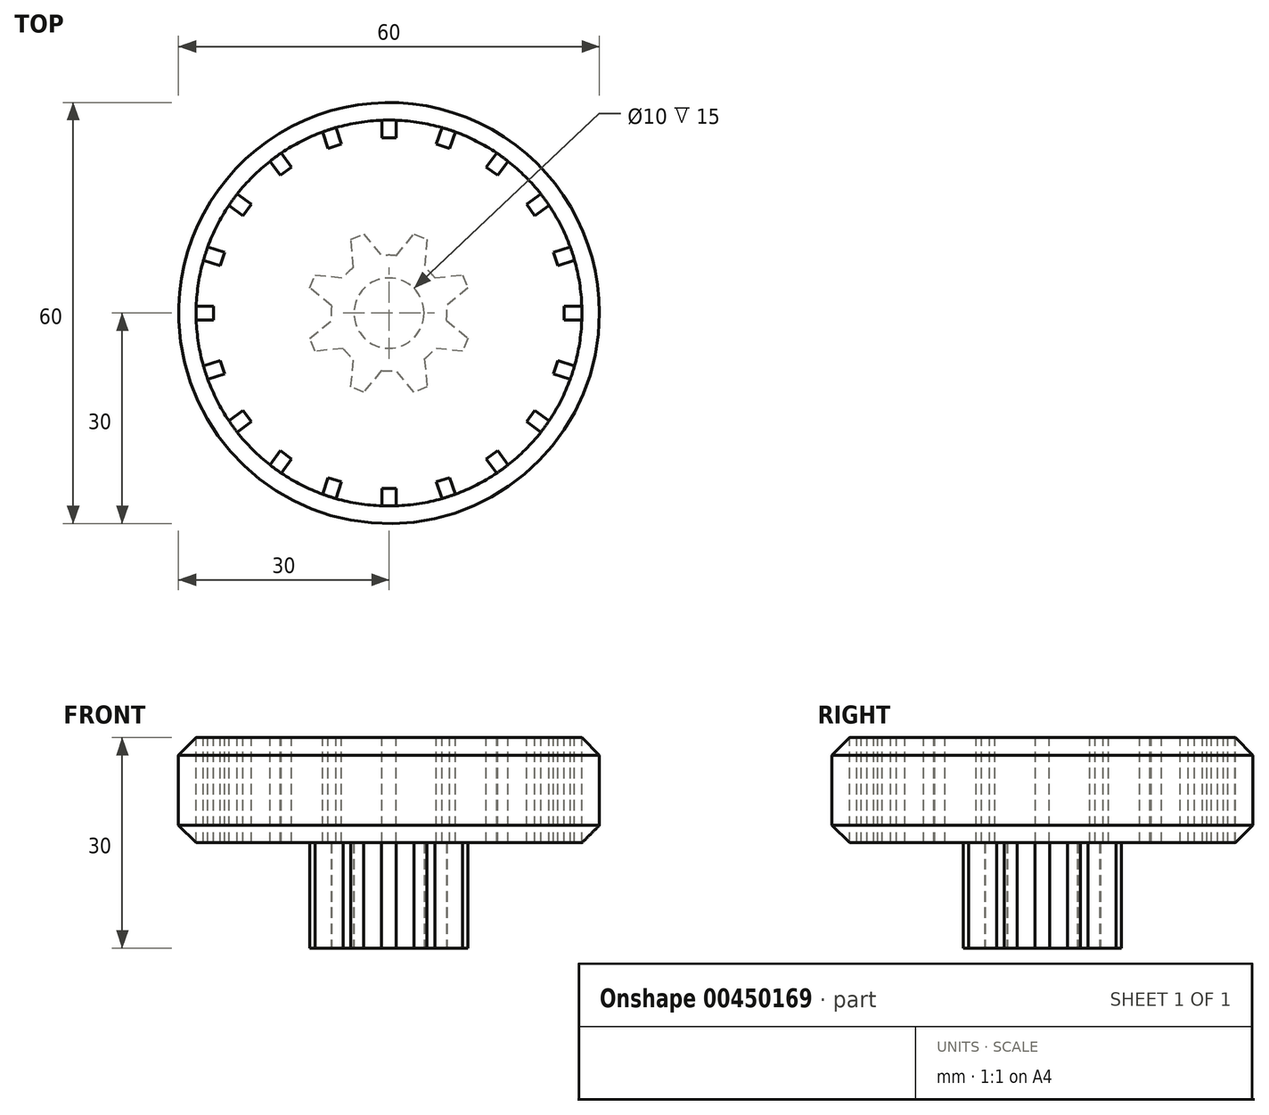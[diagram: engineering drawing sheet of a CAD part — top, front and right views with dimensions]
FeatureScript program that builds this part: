
annotation { "Feature Type Name" : "Feature", "Feature Type Description" : "" }
export const myFeature = defineFeature(function(context is Context, id is Id, definition is map)
    precondition{}
    {
        {
            var Q0;
            Q0=qCreatedBy(makeId("Top.planeOp"),FACE);
            var sketch = newSketch(context, id + "F0", { "sketchPlane" : qUnion([Q0])});
            skLineSegment(sketch, "E0", {"start": v(-8.18, 1.05) * mm, "end": v(-11.27, 3.59) * mm});
            skLineSegment(sketch, "E1", {"start": v(-11.27, 3.59) * mm, "end": v(-10.5, 5.43) * mm});
            skLineSegment(sketch, "E2", {"start": v(-10.5, 5.43) * mm, "end": v(-6.53, 5.05) * mm});
            skCircle(sketch, "E3", {"center": v(0, 0) * mm, "radius": 10 * mm, "construction": true});
            skPoint(sketch, "E4", {"position": v(-8.52, 5.24) * mm});
            skPoint(sketch, "E5", {"position": v(-9.73, 2.32) * mm});
            skArc(sketch, "E6", {"start": v(-5.05, 6.53) * mm, "mid": v(-5.83, 5.83) * mm, "end": v(-6.53, 5.05) * mm});
            skPoint(sketch, "E7", {"position": v(-11.82, 0) * mm});
            skLineSegment(sketch, "E8.1.0", {"start": v(-6.53, -5.05) * mm, "end": v(-10.5, -5.43) * mm});
            skLineSegment(sketch, "E8.1.1", {"start": v(-11.27, -3.59) * mm, "end": v(-8.18, -1.05) * mm});
            skArc(sketch, "E8.1.2", {"start": v(-8.18, 1.05) * mm, "mid": v(-8.25, 0) * mm, "end": v(-8.18, -1.05) * mm});
            skPoint(sketch, "E8.1.3", {"position": v(-9.73, -2.32) * mm});
            skPoint(sketch, "E8.1.4", {"position": v(-8.52, -5.24) * mm});
            skPoint(sketch, "E8.1.5", {"position": v(-8.36, -8.36) * mm});
            skLineSegment(sketch, "E8.1.6", {"start": v(-10.5, -5.43) * mm, "end": v(-11.27, -3.59) * mm});
            skLineSegment(sketch, "E8.2.0", {"start": v(-1.05, -8.18) * mm, "end": v(-3.59, -11.27) * mm});
            skLineSegment(sketch, "E8.2.1", {"start": v(-5.43, -10.5) * mm, "end": v(-5.05, -6.53) * mm});
            skArc(sketch, "E8.2.2", {"start": v(-6.53, -5.05) * mm, "mid": v(-5.83, -5.83) * mm, "end": v(-5.05, -6.53) * mm});
            skPoint(sketch, "E8.2.3", {"position": v(-5.24, -8.52) * mm});
            skPoint(sketch, "E8.2.4", {"position": v(-2.32, -9.73) * mm});
            skPoint(sketch, "E8.2.5", {"position": v(0, -11.82) * mm});
            skLineSegment(sketch, "E8.2.6", {"start": v(-3.59, -11.27) * mm, "end": v(-5.43, -10.5) * mm});
            skLineSegment(sketch, "E8.3.0", {"start": v(5.05, -6.53) * mm, "end": v(5.43, -10.5) * mm});
            skLineSegment(sketch, "E8.3.1", {"start": v(3.59, -11.27) * mm, "end": v(1.05, -8.18) * mm});
            skArc(sketch, "E8.3.2", {"start": v(-1.05, -8.18) * mm, "mid": v(0, -8.25) * mm, "end": v(1.05, -8.18) * mm});
            skPoint(sketch, "E8.3.3", {"position": v(2.32, -9.73) * mm});
            skPoint(sketch, "E8.3.4", {"position": v(5.24, -8.52) * mm});
            skPoint(sketch, "E8.3.5", {"position": v(8.36, -8.36) * mm});
            skLineSegment(sketch, "E8.3.6", {"start": v(5.43, -10.5) * mm, "end": v(3.59, -11.27) * mm});
            skLineSegment(sketch, "E8.4.0", {"start": v(8.18, -1.05) * mm, "end": v(11.27, -3.59) * mm});
            skLineSegment(sketch, "E8.4.1", {"start": v(10.5, -5.43) * mm, "end": v(6.53, -5.05) * mm});
            skArc(sketch, "E8.4.2", {"start": v(5.05, -6.53) * mm, "mid": v(5.83, -5.83) * mm, "end": v(6.53, -5.05) * mm});
            skPoint(sketch, "E8.4.3", {"position": v(8.52, -5.24) * mm});
            skPoint(sketch, "E8.4.4", {"position": v(9.73, -2.32) * mm});
            skPoint(sketch, "E8.4.5", {"position": v(11.82, 0) * mm});
            skLineSegment(sketch, "E8.4.6", {"start": v(11.27, -3.59) * mm, "end": v(10.5, -5.43) * mm});
            skLineSegment(sketch, "E8.5.0", {"start": v(6.53, 5.05) * mm, "end": v(10.5, 5.43) * mm});
            skLineSegment(sketch, "E8.5.1", {"start": v(11.27, 3.59) * mm, "end": v(8.18, 1.05) * mm});
            skArc(sketch, "E8.5.2", {"start": v(8.18, -1.05) * mm, "mid": v(8.25, 0) * mm, "end": v(8.18, 1.05) * mm});
            skPoint(sketch, "E8.5.3", {"position": v(9.73, 2.32) * mm});
            skPoint(sketch, "E8.5.4", {"position": v(8.52, 5.24) * mm});
            skPoint(sketch, "E8.5.5", {"position": v(8.36, 8.36) * mm});
            skLineSegment(sketch, "E8.5.6", {"start": v(10.5, 5.43) * mm, "end": v(11.27, 3.59) * mm});
            skLineSegment(sketch, "E8.6.0", {"start": v(1.05, 8.18) * mm, "end": v(3.59, 11.27) * mm});
            skLineSegment(sketch, "E8.6.1", {"start": v(5.43, 10.5) * mm, "end": v(5.05, 6.53) * mm});
            skArc(sketch, "E8.6.2", {"start": v(6.53, 5.05) * mm, "mid": v(5.83, 5.83) * mm, "end": v(5.05, 6.53) * mm});
            skPoint(sketch, "E8.6.3", {"position": v(5.24, 8.52) * mm});
            skPoint(sketch, "E8.6.4", {"position": v(2.32, 9.73) * mm});
            skPoint(sketch, "E8.6.5", {"position": v(0, 11.82) * mm});
            skLineSegment(sketch, "E8.6.6", {"start": v(3.59, 11.27) * mm, "end": v(5.43, 10.5) * mm});
            skLineSegment(sketch, "E8.7.0", {"start": v(-5.05, 6.53) * mm, "end": v(-5.43, 10.5) * mm});
            skLineSegment(sketch, "E8.7.1", {"start": v(-3.59, 11.27) * mm, "end": v(-1.05, 8.18) * mm});
            skArc(sketch, "E8.7.2", {"start": v(1.05, 8.18) * mm, "mid": v(0, 8.25) * mm, "end": v(-1.05, 8.18) * mm});
            skPoint(sketch, "E8.7.3", {"position": v(-2.32, 9.73) * mm});
            skPoint(sketch, "E8.7.4", {"position": v(-5.24, 8.52) * mm});
            skPoint(sketch, "E8.7.5", {"position": v(-8.36, 8.36) * mm});
            skLineSegment(sketch, "E8.7.6", {"start": v(-5.43, 10.5) * mm, "end": v(-3.59, 11.27) * mm});
            skCircle(sketch, "E9", {"center": v(0, 0) * mm, "radius": 5 * mm});
            skCircle(sketch, "E10", {"center": v(0, 0) * mm, "radius": 4.5 * mm});
            skPoint(sketch, "E11", {"position": v(0, 8.25) * mm});
            skSolve(sketch);
        }
        {
            var Q0;
            Q0=qSketchRegion(id+"F0",true);
            extrude(context, id + "F1", {"entities" : qUnion([Q0]), "endBound" : BoundingType.SYMMETRIC, "depth" : 15 * mm});
        }
        {
            var Q0;
            {var subQ0=sQuery(id+"F0.wireOp",EDGE,"E9");Q0=makeQuery(id+"FjRsnNbBz0NxSXN_1.boolean.opBoolean","MERGE",FACE,{"derivedFrom":[makeQuery(id+"F1.opExtrude","CAP_FACE",FACE,{"disambiguationData":[OSD([sQuery(id+"F0.wireOp",EDGE,"E0"),sQuery(id+"F0.wireOp",EDGE,"E1"),sQuery(id+"F0.wireOp",EDGE,"E2"),sQuery(id+"F0.wireOp",EDGE,"E6"),sQuery(id+"F0.wireOp",EDGE,"E8.1.0"),sQuery(id+"F0.wireOp",EDGE,"E8.1.1"),sQuery(id+"F0.wireOp",EDGE,"E8.1.2"),sQuery(id+"F0.wireOp",EDGE,"E8.1.6"),sQuery(id+"F0.wireOp",EDGE,"E8.2.0"),sQuery(id+"F0.wireOp",EDGE,"E8.2.1"),sQuery(id+"F0.wireOp",EDGE,"E8.2.2"),sQuery(id+"F0.wireOp",EDGE,"E8.2.6"),sQuery(id+"F0.wireOp",EDGE,"E8.3.0"),sQuery(id+"F0.wireOp",EDGE,"E8.3.1"),sQuery(id+"F0.wireOp",EDGE,"E8.3.2"),sQuery(id+"F0.wireOp",EDGE,"E8.3.6"),sQuery(id+"F0.wireOp",EDGE,"E8.4.0"),sQuery(id+"F0.wireOp",EDGE,"E8.4.1"),sQuery(id+"F0.wireOp",EDGE,"E8.4.2"),sQuery(id+"F0.wireOp",EDGE,"E8.4.6"),sQuery(id+"F0.wireOp",EDGE,"E8.5.0"),sQuery(id+"F0.wireOp",EDGE,"E8.5.1"),sQuery(id+"F0.wireOp",EDGE,"E8.5.2"),sQuery(id+"F0.wireOp",EDGE,"E8.5.6"),sQuery(id+"F0.wireOp",EDGE,"E8.6.0"),sQuery(id+"F0.wireOp",EDGE,"E8.6.1"),sQuery(id+"F0.wireOp",EDGE,"E8.6.2"),sQuery(id+"F0.wireOp",EDGE,"E8.6.6"),sQuery(id+"F0.wireOp",EDGE,"E8.7.0"),sQuery(id+"F0.wireOp",EDGE,"E8.7.1"),sQuery(id+"F0.wireOp",EDGE,"E8.7.2"),sQuery(id+"F0.wireOp",EDGE,"E8.7.6"),subQ0])],"isStart":false}),makeQuery(id+"FjRsnNbBz0NxSXN_1.opExtrude","CAP_FACE",FACE,{"disambiguationData":[OSD([subQ0,sQuery(id+"F0.wireOp",EDGE,"E10")])],"isStart":false})]});}
            var sketch = newSketch(context, id + "F2", { "sketchPlane" : qUnion([Q0])});
            skCircle(sketch, "E12", {"center": v(0, 0) * mm, "radius": 30 * mm});
            skSolve(sketch);
        }
        {
            var Q0;
            Q0=qSketchRegion(id+"F2",true);
            extrude(context, id + "F3", {"entities" : qUnion([Q0]), "operationType" : NewBodyOperationType.ADD, "depth" : 15 * mm});
        }
        {
            var Q0;
            Q0=makeQuery(id+"F3.opExtrude","CAP_EDGE",EDGE,{"disambiguationData":[OSD([sQuery(id+"F2.wireOp",EDGE,"E12")])],"isStart":false});
            var Q1;
            Q1=makeQuery(id+"F3.opExtrude","CAP_EDGE",EDGE,{"disambiguationData":[OSD([sQuery(id+"F2.wireOp",EDGE,"E12")])],"isStart":true});
            chamfer(context, id + "F4", {"entities" : qUnion([Q0, Q1]), "width" : 2.5 * mm, "tangentPropagation" : true});
        }
        {
            var Q0;
            Q0=makeQuery(id+"F3.opExtrude","CAP_FACE",FACE,{"disambiguationData":[OSD([sQuery(id+"F2.wireOp",EDGE,"E12")])],"isStart":false});
            var sketch = newSketch(context, id + "F5", { "sketchPlane" : qUnion([Q0])});
            skLineSegment(sketch, "E13.top", {"start": v(1, 24.98) * mm, "end": v(-1, 24.98) * mm});
            skLineSegment(sketch, "E13.left", {"start": v(1, 27.48) * mm, "end": v(1, 24.98) * mm});
            skLineSegment(sketch, "E13.right", {"start": v(-1, 27.48) * mm, "end": v(-1, 24.98) * mm});
            skPoint(sketch, "E13.middle", {"position": v(0, 26.23) * mm});
            skArc(sketch, "E14", {"start": v(1, 27.48) * mm, "mid": v(0, 27.5) * mm, "end": v(-1, 27.48) * mm});
            skLineSegment(sketch, "E15.1.0", {"start": v(-9.44, 25.83) * mm, "end": v(-8.67, 23.45) * mm});
            skPoint(sketch, "E15.1.1", {"position": v(-8.1, 24.95) * mm});
            skLineSegment(sketch, "E15.1.2", {"start": v(-7.54, 26.45) * mm, "end": v(-6.77, 24.07) * mm});
            skLineSegment(sketch, "E15.1.3", {"start": v(-6.77, 24.07) * mm, "end": v(-8.67, 23.45) * mm});
            skArc(sketch, "E15.1.4", {"start": v(-7.54, 26.45) * mm, "mid": v(-8.5, 26.15) * mm, "end": v(-9.44, 25.83) * mm});
            skLineSegment(sketch, "E15.2.0", {"start": v(-16.96, 21.65) * mm, "end": v(-15.5, 19.62) * mm});
            skPoint(sketch, "E15.2.1", {"position": v(-15.42, 21.22) * mm});
            skLineSegment(sketch, "E15.2.2", {"start": v(-15.34, 22.82) * mm, "end": v(-13.87, 20.8) * mm});
            skLineSegment(sketch, "E15.2.3", {"start": v(-13.87, 20.8) * mm, "end": v(-15.5, 19.62) * mm});
            skArc(sketch, "E15.2.4", {"start": v(-15.34, 22.82) * mm, "mid": v(-16.16, 22.25) * mm, "end": v(-16.96, 21.65) * mm});
            skLineSegment(sketch, "E15.3.0", {"start": v(-22.82, 15.34) * mm, "end": v(-20.8, 13.87) * mm});
            skPoint(sketch, "E15.3.1", {"position": v(-21.22, 15.42) * mm});
            skLineSegment(sketch, "E15.3.2", {"start": v(-21.65, 16.96) * mm, "end": v(-19.62, 15.5) * mm});
            skLineSegment(sketch, "E15.3.3", {"start": v(-19.62, 15.5) * mm, "end": v(-20.8, 13.87) * mm});
            skArc(sketch, "E15.3.4", {"start": v(-21.65, 16.96) * mm, "mid": v(-22.25, 16.16) * mm, "end": v(-22.82, 15.34) * mm});
            skLineSegment(sketch, "E15.4.0", {"start": v(-26.45, 7.54) * mm, "end": v(-24.07, 6.77) * mm});
            skPoint(sketch, "E15.4.1", {"position": v(-24.95, 8.1) * mm});
            skLineSegment(sketch, "E15.4.2", {"start": v(-25.83, 9.44) * mm, "end": v(-23.45, 8.67) * mm});
            skLineSegment(sketch, "E15.4.3", {"start": v(-23.45, 8.67) * mm, "end": v(-24.07, 6.77) * mm});
            skArc(sketch, "E15.4.4", {"start": v(-25.83, 9.44) * mm, "mid": v(-26.15, 8.5) * mm, "end": v(-26.45, 7.54) * mm});
            skLineSegment(sketch, "E15.5.0", {"start": v(-27.48, -1) * mm, "end": v(-24.98, -1) * mm});
            skPoint(sketch, "E15.5.1", {"position": v(-26.23, 0) * mm});
            skLineSegment(sketch, "E15.5.2", {"start": v(-27.48, 1) * mm, "end": v(-24.98, 1) * mm});
            skLineSegment(sketch, "E15.5.3", {"start": v(-24.98, 1) * mm, "end": v(-24.98, -1) * mm});
            skArc(sketch, "E15.5.4", {"start": v(-27.48, 1) * mm, "mid": v(-27.5, 0) * mm, "end": v(-27.48, -1) * mm});
            skLineSegment(sketch, "E15.6.0", {"start": v(-25.83, -9.44) * mm, "end": v(-23.45, -8.67) * mm});
            skPoint(sketch, "E15.6.1", {"position": v(-24.95, -8.1) * mm});
            skLineSegment(sketch, "E15.6.2", {"start": v(-26.45, -7.54) * mm, "end": v(-24.07, -6.77) * mm});
            skLineSegment(sketch, "E15.6.3", {"start": v(-24.07, -6.77) * mm, "end": v(-23.45, -8.67) * mm});
            skArc(sketch, "E15.6.4", {"start": v(-26.45, -7.54) * mm, "mid": v(-26.15, -8.5) * mm, "end": v(-25.83, -9.44) * mm});
            skLineSegment(sketch, "E15.7.0", {"start": v(-21.65, -16.96) * mm, "end": v(-19.62, -15.5) * mm});
            skPoint(sketch, "E15.7.1", {"position": v(-21.22, -15.42) * mm});
            skLineSegment(sketch, "E15.7.2", {"start": v(-22.82, -15.34) * mm, "end": v(-20.8, -13.87) * mm});
            skLineSegment(sketch, "E15.7.3", {"start": v(-20.8, -13.87) * mm, "end": v(-19.62, -15.5) * mm});
            skArc(sketch, "E15.7.4", {"start": v(-22.82, -15.34) * mm, "mid": v(-22.25, -16.16) * mm, "end": v(-21.65, -16.96) * mm});
            skLineSegment(sketch, "E15.8.0", {"start": v(-15.34, -22.82) * mm, "end": v(-13.87, -20.8) * mm});
            skPoint(sketch, "E15.8.1", {"position": v(-15.42, -21.22) * mm});
            skLineSegment(sketch, "E15.8.2", {"start": v(-16.96, -21.65) * mm, "end": v(-15.5, -19.62) * mm});
            skLineSegment(sketch, "E15.8.3", {"start": v(-15.5, -19.62) * mm, "end": v(-13.87, -20.8) * mm});
            skArc(sketch, "E15.8.4", {"start": v(-16.96, -21.65) * mm, "mid": v(-16.16, -22.25) * mm, "end": v(-15.34, -22.82) * mm});
            skLineSegment(sketch, "E15.9.0", {"start": v(-7.54, -26.45) * mm, "end": v(-6.77, -24.07) * mm});
            skPoint(sketch, "E15.9.1", {"position": v(-8.1, -24.95) * mm});
            skLineSegment(sketch, "E15.9.2", {"start": v(-9.44, -25.83) * mm, "end": v(-8.67, -23.45) * mm});
            skLineSegment(sketch, "E15.9.3", {"start": v(-8.67, -23.45) * mm, "end": v(-6.77, -24.07) * mm});
            skArc(sketch, "E15.9.4", {"start": v(-9.44, -25.83) * mm, "mid": v(-8.5, -26.15) * mm, "end": v(-7.54, -26.45) * mm});
            skLineSegment(sketch, "E15.10.0", {"start": v(1, -27.48) * mm, "end": v(1, -24.98) * mm});
            skPoint(sketch, "E15.10.1", {"position": v(0, -26.23) * mm});
            skLineSegment(sketch, "E15.10.2", {"start": v(-1, -27.48) * mm, "end": v(-1, -24.98) * mm});
            skLineSegment(sketch, "E15.10.3", {"start": v(-1, -24.98) * mm, "end": v(1, -24.98) * mm});
            skArc(sketch, "E15.10.4", {"start": v(-1, -27.48) * mm, "mid": v(0, -27.5) * mm, "end": v(1, -27.48) * mm});
            skLineSegment(sketch, "E15.11.0", {"start": v(9.44, -25.83) * mm, "end": v(8.67, -23.45) * mm});
            skPoint(sketch, "E15.11.1", {"position": v(8.1, -24.95) * mm});
            skLineSegment(sketch, "E15.11.2", {"start": v(7.54, -26.45) * mm, "end": v(6.77, -24.07) * mm});
            skLineSegment(sketch, "E15.11.3", {"start": v(6.77, -24.07) * mm, "end": v(8.67, -23.45) * mm});
            skArc(sketch, "E15.11.4", {"start": v(7.54, -26.45) * mm, "mid": v(8.5, -26.15) * mm, "end": v(9.44, -25.83) * mm});
            skLineSegment(sketch, "E15.12.0", {"start": v(16.96, -21.65) * mm, "end": v(15.5, -19.62) * mm});
            skPoint(sketch, "E15.12.1", {"position": v(15.42, -21.22) * mm});
            skLineSegment(sketch, "E15.12.2", {"start": v(15.34, -22.82) * mm, "end": v(13.87, -20.8) * mm});
            skLineSegment(sketch, "E15.12.3", {"start": v(13.87, -20.8) * mm, "end": v(15.5, -19.62) * mm});
            skArc(sketch, "E15.12.4", {"start": v(15.34, -22.82) * mm, "mid": v(16.16, -22.25) * mm, "end": v(16.96, -21.65) * mm});
            skLineSegment(sketch, "E15.13.0", {"start": v(22.82, -15.34) * mm, "end": v(20.8, -13.87) * mm});
            skPoint(sketch, "E15.13.1", {"position": v(21.22, -15.42) * mm});
            skLineSegment(sketch, "E15.13.2", {"start": v(21.65, -16.96) * mm, "end": v(19.62, -15.5) * mm});
            skLineSegment(sketch, "E15.13.3", {"start": v(19.62, -15.5) * mm, "end": v(20.8, -13.87) * mm});
            skArc(sketch, "E15.13.4", {"start": v(21.65, -16.96) * mm, "mid": v(22.25, -16.16) * mm, "end": v(22.82, -15.34) * mm});
            skLineSegment(sketch, "E15.14.0", {"start": v(26.45, -7.54) * mm, "end": v(24.07, -6.77) * mm});
            skPoint(sketch, "E15.14.1", {"position": v(24.95, -8.1) * mm});
            skLineSegment(sketch, "E15.14.2", {"start": v(25.83, -9.44) * mm, "end": v(23.45, -8.67) * mm});
            skLineSegment(sketch, "E15.14.3", {"start": v(23.45, -8.67) * mm, "end": v(24.07, -6.77) * mm});
            skArc(sketch, "E15.14.4", {"start": v(25.83, -9.44) * mm, "mid": v(26.15, -8.5) * mm, "end": v(26.45, -7.54) * mm});
            skLineSegment(sketch, "E15.15.0", {"start": v(27.48, 1) * mm, "end": v(24.98, 1) * mm});
            skPoint(sketch, "E15.15.1", {"position": v(26.23, 0) * mm});
            skLineSegment(sketch, "E15.15.2", {"start": v(27.48, -1) * mm, "end": v(24.98, -1) * mm});
            skLineSegment(sketch, "E15.15.3", {"start": v(24.98, -1) * mm, "end": v(24.98, 1) * mm});
            skArc(sketch, "E15.15.4", {"start": v(27.48, -1) * mm, "mid": v(27.5, 0) * mm, "end": v(27.48, 1) * mm});
            skLineSegment(sketch, "E15.16.0", {"start": v(25.83, 9.44) * mm, "end": v(23.45, 8.67) * mm});
            skPoint(sketch, "E15.16.1", {"position": v(24.95, 8.1) * mm});
            skLineSegment(sketch, "E15.16.2", {"start": v(26.45, 7.54) * mm, "end": v(24.07, 6.77) * mm});
            skLineSegment(sketch, "E15.16.3", {"start": v(24.07, 6.77) * mm, "end": v(23.45, 8.67) * mm});
            skArc(sketch, "E15.16.4", {"start": v(26.45, 7.54) * mm, "mid": v(26.15, 8.5) * mm, "end": v(25.83, 9.44) * mm});
            skLineSegment(sketch, "E15.17.0", {"start": v(21.65, 16.96) * mm, "end": v(19.62, 15.5) * mm});
            skPoint(sketch, "E15.17.1", {"position": v(21.22, 15.42) * mm});
            skLineSegment(sketch, "E15.17.2", {"start": v(22.82, 15.34) * mm, "end": v(20.8, 13.87) * mm});
            skLineSegment(sketch, "E15.17.3", {"start": v(20.8, 13.87) * mm, "end": v(19.62, 15.5) * mm});
            skArc(sketch, "E15.17.4", {"start": v(22.82, 15.34) * mm, "mid": v(22.25, 16.16) * mm, "end": v(21.65, 16.96) * mm});
            skLineSegment(sketch, "E15.18.0", {"start": v(15.34, 22.82) * mm, "end": v(13.87, 20.8) * mm});
            skPoint(sketch, "E15.18.1", {"position": v(15.42, 21.22) * mm});
            skLineSegment(sketch, "E15.18.2", {"start": v(16.96, 21.65) * mm, "end": v(15.5, 19.62) * mm});
            skLineSegment(sketch, "E15.18.3", {"start": v(15.5, 19.62) * mm, "end": v(13.87, 20.8) * mm});
            skArc(sketch, "E15.18.4", {"start": v(16.96, 21.65) * mm, "mid": v(16.16, 22.25) * mm, "end": v(15.34, 22.82) * mm});
            skLineSegment(sketch, "E15.19.0", {"start": v(7.54, 26.45) * mm, "end": v(6.77, 24.07) * mm});
            skPoint(sketch, "E15.19.1", {"position": v(8.1, 24.95) * mm});
            skLineSegment(sketch, "E15.19.2", {"start": v(9.44, 25.83) * mm, "end": v(8.67, 23.45) * mm});
            skLineSegment(sketch, "E15.19.3", {"start": v(8.67, 23.45) * mm, "end": v(6.77, 24.07) * mm});
            skArc(sketch, "E15.19.4", {"start": v(9.44, 25.83) * mm, "mid": v(8.5, 26.15) * mm, "end": v(7.54, 26.45) * mm});
            skSolve(sketch);
        }
        {
            var Q0;
            Q0 = qSketchRegion(id + "F5", true);
            extrude(context, id + "F6", {"entities" : qUnion([Q0]), "operationType" : NewBodyOperationType.REMOVE, "oppositeDirection" : true, "depth" : 25 * mm});
        }
    });
